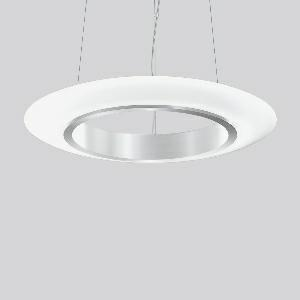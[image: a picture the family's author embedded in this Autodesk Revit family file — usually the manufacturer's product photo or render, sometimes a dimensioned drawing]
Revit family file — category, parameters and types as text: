
# Revit family: ring_of_fire_p_312546_004_730_4b3f
name_source: partatom
category: Lighting Fixtures
units: mm (PartAtom-declared; Revit-internal decimal feet)

## family parameters
Cut with Voids When Loaded = No
Host = Face
Light Source = No
Part Type = Normal
Room Calculation Point = No
Round Connector Dimension = Use Diameter
Shared = No

## types (1)
- RING OF FIRE P (1 x LED Modul 830, 5550 lm, 3000)
    Apparent Load = 71 VA
    CIE Flux Codes = 43 72 90 52 100
    Color Rendering = 80
    Color Temperature = 3000
    Default Elevation = 1800 mm
    Description = Series: RING OF FIRE
A uniquely shaped pendant luminaire with elliptical glass. Supporting ring made of anodised aluminium. Canopy aluminium anodised. Opal glass: mouth-blown, satin finish. Suitable for pendant. 3-point steel cable suspension, steplessly adjustable. Special lengths available on request. 
Colour: anodised aluminium
Diameter: 690 mm
Height: 81 mm
Suspension length: 500-1200 mm
Lamp: LED
Socket: without socket
Colour temperature: 3000K
Colour rendering index (CRI): 80
System power: 71 W
Rated luminous flux: 5550 lm
Luminous efficiency: 78 lm/W
Control gear: Dimmable Bluetooth converter
Protection class: I
Type of protection: IP 20
    Height = 81 mm
    Lamp = 1 x LED Modul 830
    Lamp Light Flux = 5550 lm
    Lamp count = 1
    Length = 690 mm
    Lifetime = 50000 h
    Luminous efficacy = 78 lm/W
    Manufacturer = RZB
    ModVariant = No
    Model = 312546.004.730
    Mounting Place = Ceiling
    Mounting Type = Pendant
    Number of Poles = 1
    OnlyDefault = Yes
    Power Factor = 1
    Product Name = RING OF FIRE P
    Product group = Pendant luminaires
    ProductGroupID = 902
    Protection Class = Protection class I
    Protection Degree = IP 20
    RLX_Detail_Level = 1
    RLX_Emergency_Light_Flux = 0 lm
    RLX_Emergency_Type = 0
    RLX_Emergency_Type_DB = No
    RlxData = <blob elided: 30177 chars, md5=17f7cbec>
    Socket = socket
    Standby Power = 0 W
    System Light Flux = 5550 lm
    System Power = 71 W
    Type Comments = Product without accessories
    Type Image = 311570.004.jpg
    URL = http://relux.com
    VarID = ---
    Voltage = 230 V
    Voltage Range = 220-240 V
    Weight = 0.00 kg
    Width = 0 mm  [stored 0 ft]

note: [stored X ft] marks values corroborated as IEEE doubles in the binary element streams (Revit-internal decimal feet)

## geometry (parser evidence)
native form markers: Blend x4, Sweep x13
no freeform markers — native parametric forms only
